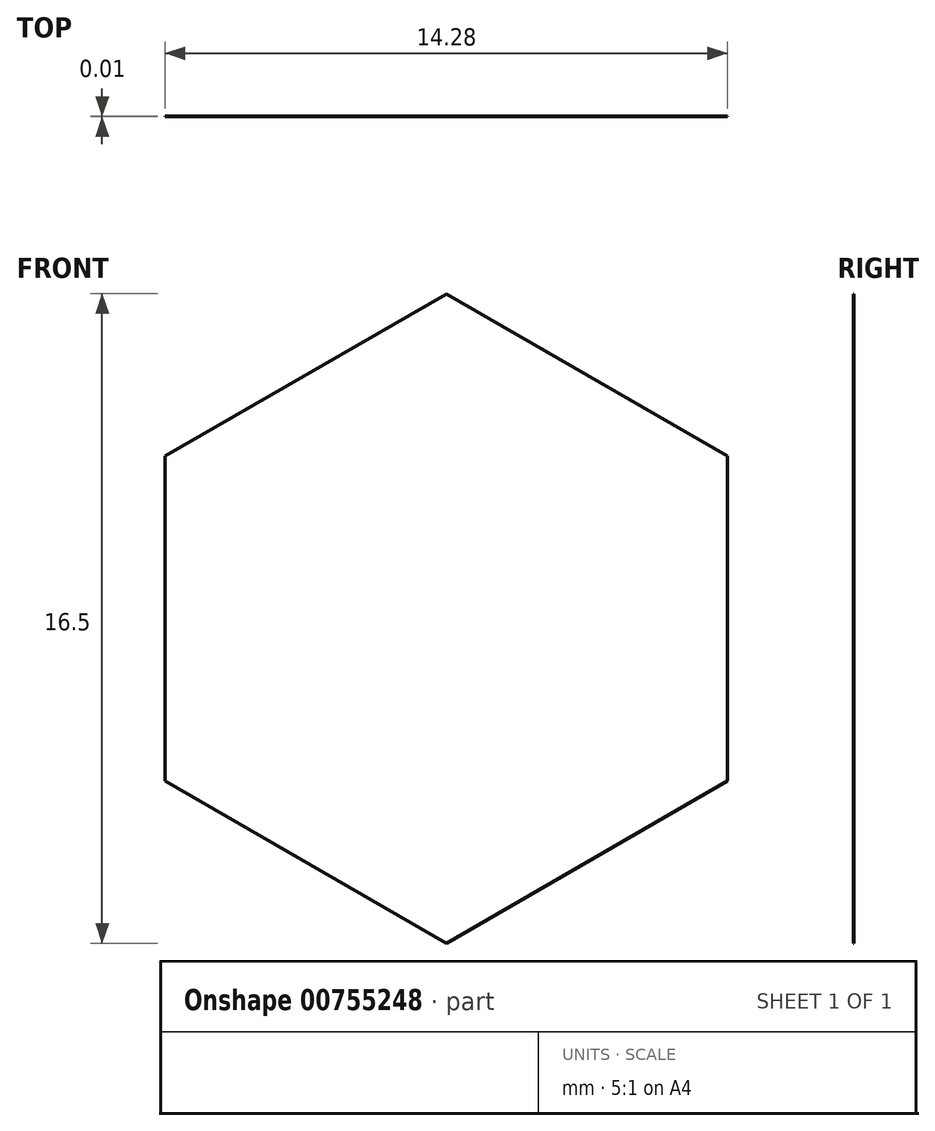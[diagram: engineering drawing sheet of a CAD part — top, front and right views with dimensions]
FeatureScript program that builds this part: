
annotation { "Feature Type Name" : "Feature", "Feature Type Description" : "" }
export const myFeature = defineFeature(function(context is Context, id is Id, definition is map)
    precondition{}
    {
        {
            var Q0;
            Q0=qCreatedBy(makeId("Front.planeOp"),FACE);
            var sketch = newSketch(context, id + "F0", { "sketchPlane" : qUnion([Q0])});
            skCircle(sketch, "E0.cCircle", {"center": v(0, 0) * mm, "radius": 7.14 * mm, "construction": true});
            skLineSegment(sketch, "E0.0", {"start": v(7.14, 4.12) * mm, "end": v(7.14, -4.12) * mm});
            skLineSegment(sketch, "E0.1", {"start": v(7.14, -4.12) * mm, "end": v(0, -8.25) * mm});
            skLineSegment(sketch, "E0.2", {"start": v(0, -8.25) * mm, "end": v(-7.14, -4.12) * mm});
            skLineSegment(sketch, "E0.3", {"start": v(-7.14, -4.12) * mm, "end": v(-7.14, 4.12) * mm});
            skLineSegment(sketch, "E0.4", {"start": v(-7.14, 4.12) * mm, "end": v(0, 8.25) * mm});
            skLineSegment(sketch, "E0.5", {"start": v(0, 8.25) * mm, "end": v(7.14, 4.12) * mm});
            skPoint(sketch, "E0.0.midPoint", {"position": v(7.14, 0) * mm});
            skSolve(sketch);
        }
        {
            var Q0;
            Q0 = qSketchRegion(id + "F0", true);
            extrude(context, id + "F1", {"entities" : qUnion([Q0]), "depth" : 21 / 1625.6 * mm, "offsetDistance" : 25.4 * mm});
        }
    });
